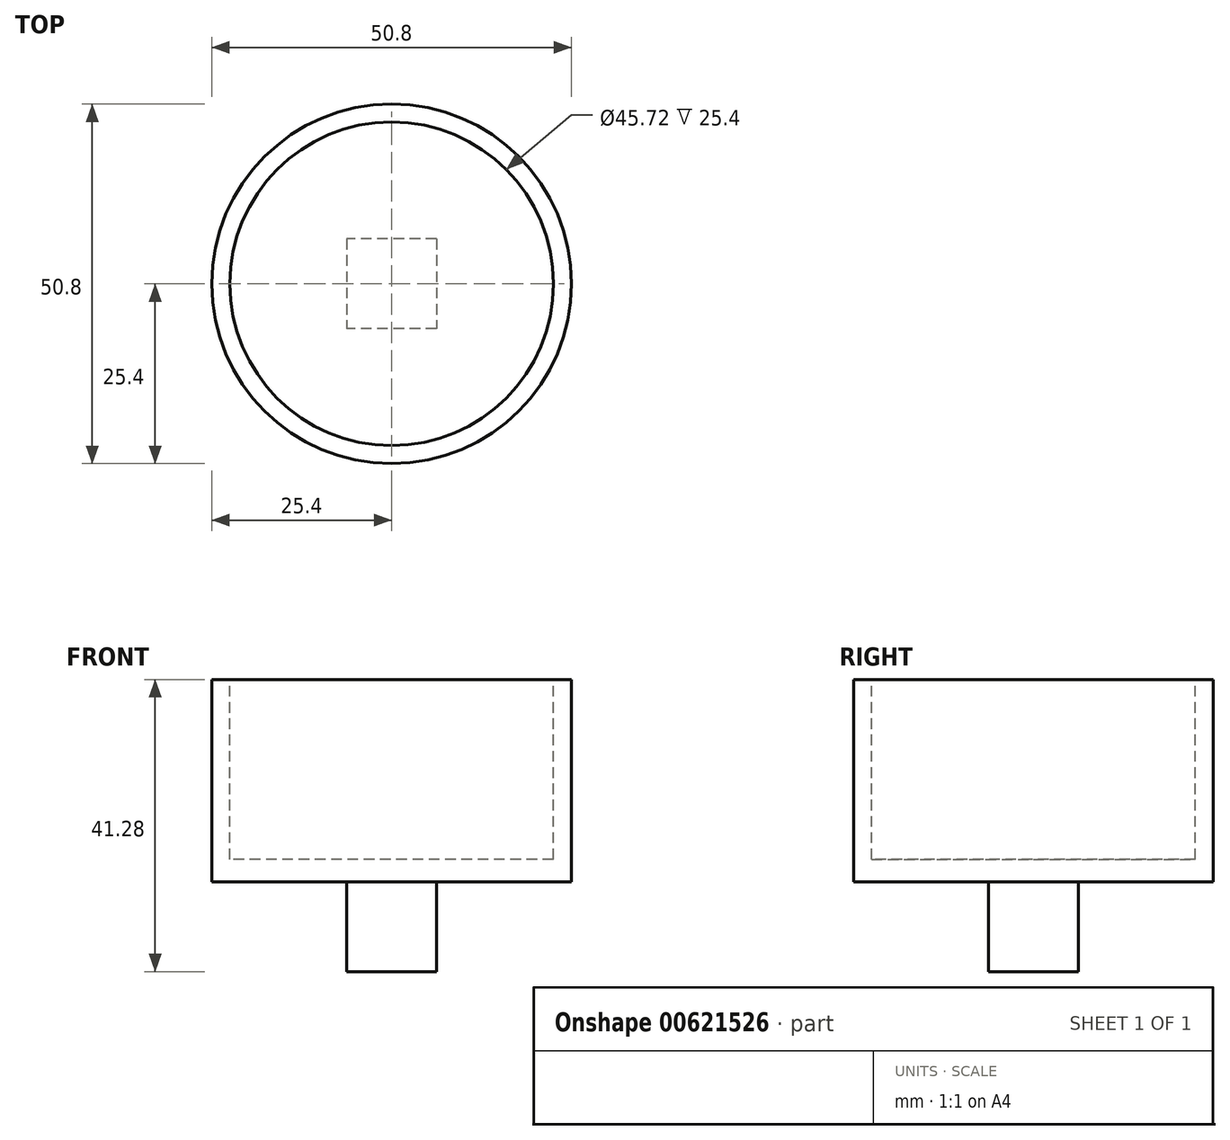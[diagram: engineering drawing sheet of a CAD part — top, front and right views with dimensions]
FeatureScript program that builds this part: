
annotation { "Feature Type Name" : "Feature", "Feature Type Description" : "" }
export const myFeature = defineFeature(function(context is Context, id is Id, definition is map)
    precondition{}
    {
        {
            var Q0;
            Q0=qCreatedBy(makeId("Top.planeOp"),FACE);
            var sketch = newSketch(context, id + "F0", { "sketchPlane" : qUnion([Q0])});
            skCircle(sketch, "E0", {"center": v(0, 0) * mm, "radius": 25.4 * mm});
            skSolve(sketch);
        }
        {
            var Q0;
            Q0 = qSketchRegion(id + "F0", true);
            extrude(context, id + "F1", {"entities" : qUnion([Q0]), "depth" : 28.57 * mm, "offsetDistance" : 25.4 * mm});
        }
        {
            var Q0;
            Q0=makeQuery(id+"F1.opExtrude","CAP_FACE",FACE,{"disambiguationData":[OSD([sQuery(id+"F0.wireOp",EDGE,"E0")])],"isStart":false});
            var sketch = newSketch(context, id + "F2", { "sketchPlane" : qUnion([Q0])});
            skCircle(sketch, "E1", {"center": v(0, 0) * mm, "radius": 22.86 * mm});
            skSolve(sketch);
        }
        {
            var Q0;
            Q0 = qSketchRegion(id + "F2", true);
            extrude(context, id + "F3", {"entities" : qUnion([Q0]), "operationType" : NewBodyOperationType.REMOVE, "oppositeDirection" : true, "depth" : 25.4 * mm, "offsetDistance" : 25.4 * mm});
        }
        {
            var Q0;
            Q0=makeQuery(id+"F1.opExtrude","CAP_FACE",FACE,{"disambiguationData":[OSD([sQuery(id+"F0.wireOp",EDGE,"E0")])],"isStart":true});
            var sketch = newSketch(context, id + "F4", { "sketchPlane" : qUnion([Q0])});
            skLineSegment(sketch, "E2.bottom", {"start": v(6.35, -6.35) * mm, "end": v(-6.35, -6.35) * mm});
            skLineSegment(sketch, "E2.top", {"start": v(6.35, 6.35) * mm, "end": v(-6.35, 6.35) * mm});
            skLineSegment(sketch, "E2.left", {"start": v(6.35, -6.35) * mm, "end": v(6.35, 6.35) * mm});
            skLineSegment(sketch, "E2.right", {"start": v(-6.35, -6.35) * mm, "end": v(-6.35, 6.35) * mm});
            skPoint(sketch, "E2.middle", {"position": v(0, 0) * mm});
            skSolve(sketch);
        }
        {
            var Q0;
            Q0 = qSketchRegion(id + "F4", true);
            extrude(context, id + "F5", {"entities" : qUnion([Q0]), "operationType" : NewBodyOperationType.ADD, "depth" : 12.7 * mm, "offsetDistance" : 25.4 * mm});
        }
    });
